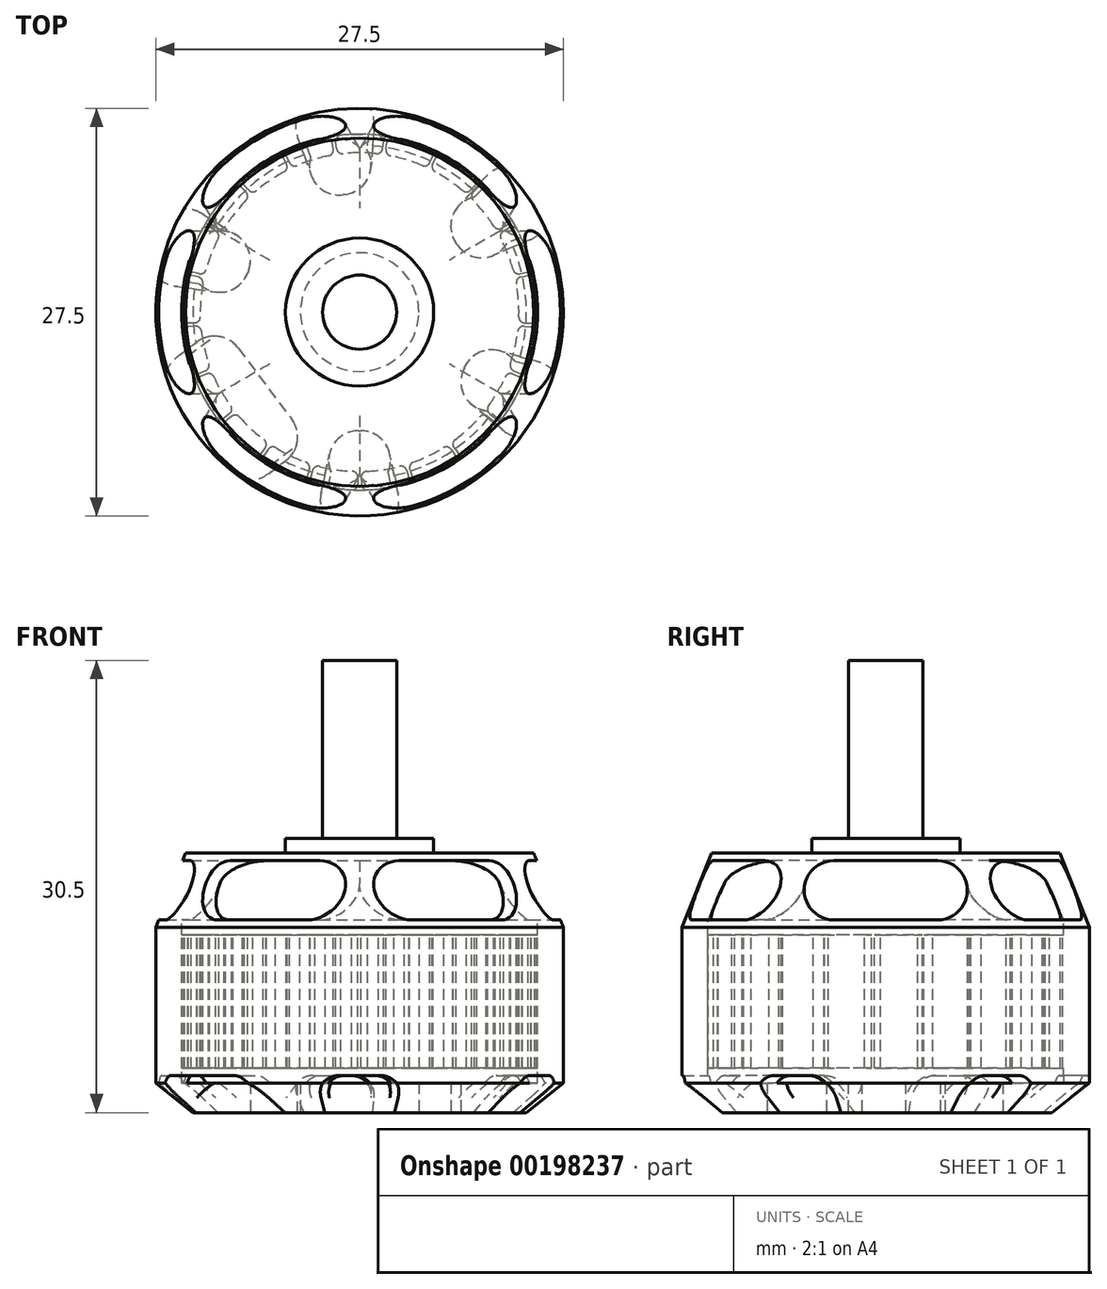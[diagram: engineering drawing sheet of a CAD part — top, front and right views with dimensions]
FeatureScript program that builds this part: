
annotation { "Feature Type Name" : "Feature", "Feature Type Description" : "" }
export const myFeature = defineFeature(function(context is Context, id is Id, definition is map)
    precondition{}
    {
        {
            var Q0;
            Q0=qCreatedBy(makeId("Top.planeOp"),FACE);
            var sketch = newSketch(context, id + "F0", { "sketchPlane" : qUnion([Q0])});
            skCircle(sketch, "E0", {"center": v(0, 0) * mm, "radius": 13.75 * mm});
            skSolve(sketch);
        }
        {
            var Q0;
            Q0=makeQuery(id+"F0.imprint","IMPRINT",FACE,{"disambiguationData":[TD([[makeQuery(id+"F0.imprint","IMPRINT",EDGE,{"derivedFrom":sQuery(id+"F0.wireOp",EDGE,"E0")}),1.0]])]});
            extrude(context, id + "F1", {"entities" : qUnion([Q0]), "depth" : 17.5 * mm});
        }
        {
            var Q0;
            Q0=makeQuery(id+"F1.opExtrude","CAP_FACE",FACE,{"disambiguationData":[OSD([sQuery(id+"F0.wireOp",EDGE,"E0")])],"isStart":false});
            var sketch = newSketch(context, id + "F2", { "sketchPlane" : qUnion([Q0])});
            skCircle(sketch, "E1", {"center": v(0, 0) * mm, "radius": 5 * mm});
            skSolve(sketch);
        }
        {
            var Q0;
            Q0=makeQuery(id+"F2.imprint","IMPRINT",FACE,{"disambiguationData":[TD([[makeQuery(id+"F2.imprint","IMPRINT",EDGE,{"derivedFrom":sQuery(id+"F2.wireOp",EDGE,"E1")}),1.0]])]});
            extrude(context, id + "F3", {"entities" : qUnion([Q0]), "operationType" : NewBodyOperationType.ADD, "depth" : 1 * mm});
        }
        {
            var Q0;
            Q0=makeQuery(id+"F3.opExtrude","CAP_FACE",FACE,{"disambiguationData":[OSD([sQuery(id+"F2.wireOp",EDGE,"E1")])],"isStart":false});
            var sketch = newSketch(context, id + "F4", { "sketchPlane" : qUnion([Q0])});
            skCircle(sketch, "E2", {"center": v(0, 0) * mm, "radius": 2.5 * mm});
            skSolve(sketch);
        }
        {
            var Q0;
            Q0=makeQuery(id+"F4.imprint","IMPRINT",FACE,{"disambiguationData":[TD([[makeQuery(id+"F4.imprint","IMPRINT",EDGE,{"derivedFrom":sQuery(id+"F4.wireOp",EDGE,"E2")}),1.0]])]});
            extrude(context, id + "F5", {"entities" : qUnion([Q0]), "operationType" : NewBodyOperationType.ADD, "depth" : 12 * mm});
        }
        {
            var Q0;
            Q0=makeQuery(id+"F1.opExtrude","CAP_EDGE",EDGE,{"disambiguationData":[OSD([sQuery(id+"F0.wireOp",EDGE,"E0")])],"isStart":false});
            chamfer(context, id + "F6", {"entities" : qUnion([Q0]), "chamferType" : ChamferType.TWO_OFFSETS, "width1" : 2 * mm, "oppositeDirection" : false, "width2" : 5 * mm, "tangentPropagation" : true});
        }
        {
            var Q0;
            Q0=makeQuery(id+"F1.opExtrude","CAP_EDGE",EDGE,{"disambiguationData":[OSD([sQuery(id+"F0.wireOp",EDGE,"E0")])],"isStart":true});
            chamfer(context, id + "F7", {"entities" : qUnion([Q0]), "chamferType" : ChamferType.TWO_OFFSETS, "width1" : 2 * mm, "oppositeDirection" : false, "width2" : 2.5 * mm, "tangentPropagation" : true});
        }
        {
            var Q0;
            Q0=qCreatedBy(makeId("Right.planeOp"),FACE);
            var sketch = newSketch(context, id + "F8", { "sketchPlane" : qUnion([Q0])});
            skLineSegment(sketch, "E3.bottom", {"start": v(-3.5, 17) * mm, "end": v(3.5, 17) * mm});
            skLineSegment(sketch, "E3.top", {"start": v(-3.5, 13) * mm, "end": v(3.5, 13) * mm});
            skLineSegment(sketch, "E3.left", {"start": v(-3.5, 17) * mm, "end": v(-3.5, 13) * mm, "construction": true});
            skLineSegment(sketch, "E3.right", {"start": v(3.5, 17) * mm, "end": v(3.5, 13) * mm, "construction": true});
            skArc(sketch, "E4", {"start": v(-3.5, 17) * mm, "mid": v(-5.5, 15) * mm, "end": v(-3.5, 13) * mm});
            skArc(sketch, "E5", {"start": v(3.5, 13) * mm, "mid": v(5.5, 15) * mm, "end": v(3.5, 17) * mm});
            skSolve(sketch);
        }
        {
            var Q0;
            Q0 = qSketchRegion(id + "F8", true);
            extrude(context, id + "F9", {"entities" : qUnion([Q0]), "endBound" : BoundingType.SYMMETRIC, "oppositeDirection" : true, "depth" : 30 * mm});
        }
        {
            var Q0;
            Q0=makeQuery(id+"F9.opExtrude","SWEPT_BODY",BODY,{"disambiguationData":[OSD([sQuery(id+"F8.wireOp",EDGE,"E3.bottom"),sQuery(id+"F8.wireOp",EDGE,"E3.top"),sQuery(id+"F8.wireOp",EDGE,"E4"),sQuery(id+"F8.wireOp",EDGE,"E5")])]});
            var Q1;
            Q1=makeQuery(id+"F5.opExtrude","SWEPT_FACE",FACE,{"disambiguationData":[OSD([sQuery(id+"F4.wireOp",EDGE,"E2")])]});
            circularPattern(context, id + "F10", {"entities" : qUnion([Q0]), "axis" : qUnion([Q1]), "angle" : 180 * degree, "instanceCount" : 4, "equalSpace" : true});
        }
        {
            var Q0;
            Q0=makeQuery(id+"F10.opPattern","COPY",BODY,{"derivedFrom":makeQuery(id+"F9.opExtrude","SWEPT_BODY",BODY,{"disambiguationData":[OSD([sQuery(id+"F8.wireOp",EDGE,"E3.bottom"),sQuery(id+"F8.wireOp",EDGE,"E3.top"),sQuery(id+"F8.wireOp",EDGE,"E4"),sQuery(id+"F8.wireOp",EDGE,"E5")])]}),"instanceName":"1"});
            var Q1;
            Q1=makeQuery(id+"F10.opPattern","COPY",BODY,{"derivedFrom":makeQuery(id+"F9.opExtrude","SWEPT_BODY",BODY,{"disambiguationData":[OSD([sQuery(id+"F8.wireOp",EDGE,"E3.bottom"),sQuery(id+"F8.wireOp",EDGE,"E3.top"),sQuery(id+"F8.wireOp",EDGE,"E4"),sQuery(id+"F8.wireOp",EDGE,"E5")])]}),"instanceName":"2"});
            var Q2;
            Q2=makeQuery(id+"F9.opExtrude","SWEPT_BODY",BODY,{"disambiguationData":[OSD([sQuery(id+"F8.wireOp",EDGE,"E3.bottom"),sQuery(id+"F8.wireOp",EDGE,"E3.top"),sQuery(id+"F8.wireOp",EDGE,"E4"),sQuery(id+"F8.wireOp",EDGE,"E5")])]});
            var Q3;
            Q3=makeQuery(id+"F10.opPattern","COPY",BODY,{"derivedFrom":makeQuery(id+"F9.opExtrude","SWEPT_BODY",BODY,{"disambiguationData":[OSD([sQuery(id+"F8.wireOp",EDGE,"E3.bottom"),sQuery(id+"F8.wireOp",EDGE,"E3.top"),sQuery(id+"F8.wireOp",EDGE,"E4"),sQuery(id+"F8.wireOp",EDGE,"E5")])]}),"instanceName":"3"});
            booleanBodies(context, id + "F11", {"operationType" : BooleanOperationType.UNION, "tools" : qUnion([Q0, Q1, Q2, Q3])});
        }
        {
            var Q0;
            Q0=makeQuery(id+"F9.opExtrude","SWEPT_BODY",BODY,{"disambiguationData":[OSD([sQuery(id+"F8.wireOp",EDGE,"E3.bottom"),sQuery(id+"F8.wireOp",EDGE,"E3.top"),sQuery(id+"F8.wireOp",EDGE,"E4"),sQuery(id+"F8.wireOp",EDGE,"E5")])]});
            var Q1;
            Q1=makeQuery(id+"F10.opPattern","COPY",BODY,{"derivedFrom":makeQuery(id+"F9.opExtrude","SWEPT_BODY",BODY,{"disambiguationData":[OSD([sQuery(id+"F8.wireOp",EDGE,"E3.bottom"),sQuery(id+"F8.wireOp",EDGE,"E3.top"),sQuery(id+"F8.wireOp",EDGE,"E4"),sQuery(id+"F8.wireOp",EDGE,"E5")])]}),"instanceName":"1"});
            var Q2;
            Q2=makeQuery(id+"F10.opPattern","COPY",BODY,{"derivedFrom":makeQuery(id+"F9.opExtrude","SWEPT_BODY",BODY,{"disambiguationData":[OSD([sQuery(id+"F8.wireOp",EDGE,"E3.bottom"),sQuery(id+"F8.wireOp",EDGE,"E3.top"),sQuery(id+"F8.wireOp",EDGE,"E4"),sQuery(id+"F8.wireOp",EDGE,"E5")])]}),"instanceName":"2"});
            var Q3;
            Q3=makeQuery(id+"F1.opExtrude","SWEPT_BODY",BODY,{"disambiguationData":[OSD([sQuery(id+"F0.wireOp",EDGE,"E0")])]});
            booleanBodies(context, id + "F12", {"operationType" : BooleanOperationType.SUBTRACTION, "tools" : qUnion([Q0, Q1, Q2]), "targets" : qUnion([Q3])});
        }
        {
            var Q0;
            Q0=qCreatedBy(makeId("Right.planeOp"),FACE);
            var sketch = newSketch(context, id + "F13", { "sketchPlane" : qUnion([Q0])});
            skLineSegment(sketch, "E6", {"start": v(10.9, 15.44) * mm, "end": v(12, 13) * mm});
            skLineSegment(sketch, "E7", {"start": v(12, 13) * mm, "end": v(12, 2) * mm});
            skLineSegment(sketch, "E8", {"start": v(12, 2) * mm, "end": v(0, 2) * mm});
            skLineSegment(sketch, "E9", {"start": v(0, 2) * mm, "end": v(0, 15.44) * mm});
            skLineSegment(sketch, "E10", {"start": v(0, 15.44) * mm, "end": v(10.9, 15.44) * mm});
            skSolve(sketch);
        }
        {
            var Q0;
            Q0 = qSketchRegion(id + "F13", true);
            var Q1;
            Q1=sQuery(id+"F13.wireOp",EDGE,"E9");
            revolve(context, id + "F14", {"operationType" : NewBodyOperationType.REMOVE, "entities" : qUnion([Q0]), "axis" : qUnion([Q1]), "revolveType" : RevolveType.FULL, "oppositeDirection" : true});
        }
        {
            var Q0;
            Q0=qCreatedBy(makeId("Top.planeOp"),FACE);
            cPlane(context, id + "F15", {"entities" : qUnion([Q0]), "cplaneType" : CPlaneType.OFFSET, "offset" : 12 * mm, "width" : 150 * mm, "height" : 150 * mm});
        }
        {
            var Q0;
            Q0=qCreatedBy(id+"F15.planeOp",FACE);
            var sketch = newSketch(context, id + "F16", { "sketchPlane" : qUnion([Q0])});
            skArc(sketch, "E11", {"start": v(1.26, 11.93) * mm, "mid": v(0, 12) * mm, "end": v(-1.26, 11.93) * mm});
            skArc(sketch, "E12", {"start": v(1.11, 10.7) * mm, "mid": v(0, 10.75) * mm, "end": v(-1.11, 10.7) * mm});
            skLineSegment(sketch, "E13", {"start": v(1.55, 11.03) * mm, "end": v(1.61, 11.48) * mm});
            skLineSegment(sketch, "E14", {"start": v(-1.55, 11.03) * mm, "end": v(-1.61, 11.48) * mm});
            skPoint(sketch, "E15.visualSharp", {"position": v(-1.5, 10.65) * mm});
            skArc(sketch, "E15.filletArc", {"start": v(-1.55, 11.03) * mm, "mid": v(-1.4, 10.77) * mm, "end": v(-1.11, 10.7) * mm});
            skPoint(sketch, "E16.visualSharp", {"position": v(1.5, 10.65) * mm});
            skArc(sketch, "E16.filletArc", {"start": v(1.11, 10.7) * mm, "mid": v(1.4, 10.77) * mm, "end": v(1.55, 11.03) * mm});
            skPoint(sketch, "E17.visualSharp", {"position": v(-1.67, 11.88) * mm});
            skArc(sketch, "E17.filletArc", {"start": v(-1.26, 11.93) * mm, "mid": v(-1.53, 11.78) * mm, "end": v(-1.61, 11.48) * mm});
            skPoint(sketch, "E18.visualSharp", {"position": v(1.67, 11.88) * mm});
            skArc(sketch, "E18.filletArc", {"start": v(1.61, 11.48) * mm, "mid": v(1.53, 11.78) * mm, "end": v(1.26, 11.93) * mm});
            skPoint(sketch, "E19.1.0", {"position": v(-1.7, 10.61) * mm});
            skPoint(sketch, "E19.1.1", {"position": v(-4.57, 9.73) * mm});
            skPoint(sketch, "E19.1.2", {"position": v(-1.9, 11.85) * mm});
            skPoint(sketch, "E19.1.3", {"position": v(-5.1, 10.86) * mm});
            skArc(sketch, "E19.1.4", {"start": v(-2.31, 11.77) * mm, "mid": v(-3.54, 11.47) * mm, "end": v(-4.72, 11.03) * mm});
            skArc(sketch, "E19.1.5", {"start": v(-2.09, 10.55) * mm, "mid": v(-3.17, 10.27) * mm, "end": v(-4.22, 9.89) * mm});
            skLineSegment(sketch, "E19.1.6", {"start": v(-1.77, 11) * mm, "end": v(-1.84, 11.45) * mm});
            skArc(sketch, "E19.1.7", {"start": v(-4.72, 11.03) * mm, "mid": v(-4.94, 10.8) * mm, "end": v(-4.93, 10.5) * mm});
            skArc(sketch, "E19.1.8", {"start": v(-4.73, 10.09) * mm, "mid": v(-4.51, 9.88) * mm, "end": v(-4.22, 9.89) * mm});
            skArc(sketch, "E19.1.9", {"start": v(-1.84, 11.45) * mm, "mid": v(-2, 11.71) * mm, "end": v(-2.31, 11.77) * mm});
            skLineSegment(sketch, "E19.1.10", {"start": v(-4.73, 10.09) * mm, "end": v(-4.93, 10.5) * mm});
            skArc(sketch, "E19.1.11", {"start": v(-2.09, 10.55) * mm, "mid": v(-1.84, 10.7) * mm, "end": v(-1.77, 11) * mm});
            skPoint(sketch, "E19.2.0", {"position": v(-4.76, 9.64) * mm});
            skPoint(sketch, "E19.2.1", {"position": v(-7.23, 7.95) * mm});
            skPoint(sketch, "E19.2.2", {"position": v(-5.31, 10.76) * mm});
            skPoint(sketch, "E19.2.3", {"position": v(-8.07, 8.88) * mm});
            skArc(sketch, "E19.2.4", {"start": v(-5.68, 10.57) * mm, "mid": v(-6.76, 9.91) * mm, "end": v(-7.76, 9.15) * mm});
            skArc(sketch, "E19.2.5", {"start": v(-5.1, 9.46) * mm, "mid": v(-6.06, 8.88) * mm, "end": v(-6.94, 8.2) * mm});
            skLineSegment(sketch, "E19.2.6", {"start": v(-4.93, 10) * mm, "end": v(-5.13, 10.4) * mm});
            skArc(sketch, "E19.2.7", {"start": v(-7.76, 9.15) * mm, "mid": v(-7.9, 8.87) * mm, "end": v(-7.8, 8.58) * mm});
            skArc(sketch, "E19.2.8", {"start": v(-7.5, 8.24) * mm, "mid": v(-7.23, 8.11) * mm, "end": v(-6.94, 8.2) * mm});
            skArc(sketch, "E19.2.9", {"start": v(-5.13, 10.4) * mm, "mid": v(-5.37, 10.6) * mm, "end": v(-5.68, 10.57) * mm});
            skLineSegment(sketch, "E19.2.10", {"start": v(-7.5, 8.24) * mm, "end": v(-7.8, 8.58) * mm});
            skArc(sketch, "E19.2.11", {"start": v(-5.1, 9.46) * mm, "mid": v(-4.91, 9.7) * mm, "end": v(-4.93, 10) * mm});
            skPoint(sketch, "E19.3.0", {"position": v(-7.4, 7.8) * mm});
            skPoint(sketch, "E19.3.1", {"position": v(-9.26, 5.47) * mm});
            skPoint(sketch, "E19.3.2", {"position": v(-8.25, 8.71) * mm});
            skPoint(sketch, "E19.3.3", {"position": v(-10.33, 6.1) * mm});
            skArc(sketch, "E19.3.4", {"start": v(-8.55, 8.43) * mm, "mid": v(-9.38, 7.48) * mm, "end": v(-10.12, 6.46) * mm});
            skArc(sketch, "E19.3.5", {"start": v(-7.67, 7.54) * mm, "mid": v(-8.4, 6.7) * mm, "end": v(-9.05, 5.8) * mm});
            skLineSegment(sketch, "E19.3.6", {"start": v(-7.66, 8.1) * mm, "end": v(-7.97, 8.42) * mm});
            skArc(sketch, "E19.3.7", {"start": v(-10.12, 6.46) * mm, "mid": v(-10.17, 6.15) * mm, "end": v(-9.98, 5.9) * mm});
            skArc(sketch, "E19.3.8", {"start": v(-9.6, 5.67) * mm, "mid": v(-9.3, 5.62) * mm, "end": v(-9.05, 5.8) * mm});
            skArc(sketch, "E19.3.9", {"start": v(-7.97, 8.42) * mm, "mid": v(-8.26, 8.54) * mm, "end": v(-8.55, 8.43) * mm});
            skLineSegment(sketch, "E19.3.10", {"start": v(-9.6, 5.67) * mm, "end": v(-9.98, 5.9) * mm});
            skArc(sketch, "E19.3.11", {"start": v(-7.67, 7.54) * mm, "mid": v(-7.55, 7.81) * mm, "end": v(-7.66, 8.1) * mm});
            skPoint(sketch, "E19.4.0", {"position": v(-9.36, 5.28) * mm});
            skPoint(sketch, "E19.4.1", {"position": v(-10.46, 2.5) * mm});
            skPoint(sketch, "E19.4.2", {"position": v(-10.45, 5.9) * mm});
            skPoint(sketch, "E19.4.3", {"position": v(-11.67, 2.79) * mm});
            skArc(sketch, "E19.4.4", {"start": v(-10.65, 5.53) * mm, "mid": v(-11.17, 4.38) * mm, "end": v(-11.57, 3.19) * mm});
            skArc(sketch, "E19.4.5", {"start": v(-9.55, 4.94) * mm, "mid": v(-10, 3.93) * mm, "end": v(-10.36, 2.87) * mm});
            skLineSegment(sketch, "E19.4.6", {"start": v(-9.7, 5.47) * mm, "end": v(-10.1, 5.7) * mm});
            skArc(sketch, "E19.4.7", {"start": v(-11.57, 3.19) * mm, "mid": v(-11.53, 2.88) * mm, "end": v(-11.28, 2.7) * mm});
            skArc(sketch, "E19.4.8", {"start": v(-10.84, 2.59) * mm, "mid": v(-10.54, 2.63) * mm, "end": v(-10.36, 2.87) * mm});
            skArc(sketch, "E19.4.9", {"start": v(-10.1, 5.7) * mm, "mid": v(-10.4, 5.73) * mm, "end": v(-10.65, 5.53) * mm});
            skLineSegment(sketch, "E19.4.10", {"start": v(-10.84, 2.59) * mm, "end": v(-11.28, 2.7) * mm});
            skArc(sketch, "E19.4.11", {"start": v(-9.55, 4.94) * mm, "mid": v(-9.52, 5.24) * mm, "end": v(-9.7, 5.47) * mm});
            skPoint(sketch, "E19.5.0", {"position": v(-10.5, 2.29) * mm});
            skPoint(sketch, "E19.5.1", {"position": v(-10.73, -0.7) * mm});
            skPoint(sketch, "E19.5.2", {"position": v(-11.73, 2.55) * mm});
            skPoint(sketch, "E19.5.3", {"position": v(-11.97, -0.78) * mm});
            skArc(sketch, "E19.5.4", {"start": v(-11.8, 2.15) * mm, "mid": v(-11.97, 0.9) * mm, "end": v(-12, -0.36) * mm});
            skArc(sketch, "E19.5.5", {"start": v(-10.58, 1.9) * mm, "mid": v(-10.72, 0.8) * mm, "end": v(-10.75, -0.31) * mm});
            skLineSegment(sketch, "E19.5.6", {"start": v(-10.89, 2.37) * mm, "end": v(-11.33, 2.47) * mm});
            skArc(sketch, "E19.5.7", {"start": v(-12, -0.36) * mm, "mid": v(-11.86, -0.65) * mm, "end": v(-11.57, -0.75) * mm});
            skArc(sketch, "E19.5.8", {"start": v(-11.12, -0.72) * mm, "mid": v(-10.85, -0.6) * mm, "end": v(-10.75, -0.31) * mm});
            skArc(sketch, "E19.5.9", {"start": v(-11.33, 2.47) * mm, "mid": v(-11.63, 2.4) * mm, "end": v(-11.8, 2.15) * mm});
            skLineSegment(sketch, "E19.5.10", {"start": v(-11.12, -0.72) * mm, "end": v(-11.57, -0.75) * mm});
            skArc(sketch, "E19.5.11", {"start": v(-10.58, 1.9) * mm, "mid": v(-10.64, 2.2) * mm, "end": v(-10.89, 2.37) * mm});
            skPoint(sketch, "E19.6.0", {"position": v(-10.71, -0.91) * mm});
            skPoint(sketch, "E19.6.1", {"position": v(-10.05, -3.83) * mm});
            skPoint(sketch, "E19.6.2", {"position": v(-11.96, -1.02) * mm});
            skPoint(sketch, "E19.6.3", {"position": v(-11.21, -4.27) * mm});
            skArc(sketch, "E19.6.4", {"start": v(-11.91, -1.43) * mm, "mid": v(-11.7, -2.67) * mm, "end": v(-11.35, -3.88) * mm});
            skArc(sketch, "E19.6.5", {"start": v(-10.67, -1.3) * mm, "mid": v(-10.48, -2.4) * mm, "end": v(-10.18, -3.46) * mm});
            skLineSegment(sketch, "E19.6.6", {"start": v(-11.1, -0.94) * mm, "end": v(-11.55, -0.98) * mm});
            skArc(sketch, "E19.6.7", {"start": v(-11.35, -3.88) * mm, "mid": v(-11.15, -4.12) * mm, "end": v(-10.83, -4.13) * mm});
            skArc(sketch, "E19.6.8", {"start": v(-10.41, -3.97) * mm, "mid": v(-10.2, -3.76) * mm, "end": v(-10.18, -3.46) * mm});
            skArc(sketch, "E19.6.9", {"start": v(-11.55, -0.98) * mm, "mid": v(-11.83, -1.13) * mm, "end": v(-11.91, -1.43) * mm});
            skLineSegment(sketch, "E19.6.10", {"start": v(-10.41, -3.97) * mm, "end": v(-10.83, -4.13) * mm});
            skArc(sketch, "E19.6.11", {"start": v(-10.67, -1.3) * mm, "mid": v(-10.82, -1.03) * mm, "end": v(-11.1, -0.94) * mm});
            skPoint(sketch, "E19.7.0", {"position": v(-9.97, -4.03) * mm});
            skPoint(sketch, "E19.7.1", {"position": v(-8.47, -6.62) * mm});
            skPoint(sketch, "E19.7.2", {"position": v(-11.13, -4.5) * mm});
            skPoint(sketch, "E19.7.3", {"position": v(-9.46, -7.39) * mm});
            skArc(sketch, "E19.7.4", {"start": v(-10.96, -4.88) * mm, "mid": v(-10.4, -6) * mm, "end": v(-9.7, -7.06) * mm});
            skArc(sketch, "E19.7.5", {"start": v(-9.82, -4.38) * mm, "mid": v(-9.3, -5.38) * mm, "end": v(-8.7, -6.31) * mm});
            skLineSegment(sketch, "E19.7.6", {"start": v(-10.33, -4.17) * mm, "end": v(-10.75, -4.34) * mm});
            skArc(sketch, "E19.7.7", {"start": v(-9.7, -7.06) * mm, "mid": v(-9.44, -7.22) * mm, "end": v(-9.14, -7.14) * mm});
            skArc(sketch, "E19.7.8", {"start": v(-8.78, -6.86) * mm, "mid": v(-8.63, -6.6) * mm, "end": v(-8.7, -6.31) * mm});
            skArc(sketch, "E19.7.9", {"start": v(-10.75, -4.34) * mm, "mid": v(-10.97, -4.56) * mm, "end": v(-10.96, -4.88) * mm});
            skLineSegment(sketch, "E19.7.10", {"start": v(-8.78, -6.86) * mm, "end": v(-9.14, -7.14) * mm});
            skArc(sketch, "E19.7.11", {"start": v(-9.82, -4.38) * mm, "mid": v(-10.03, -4.17) * mm, "end": v(-10.33, -4.17) * mm});
            skPoint(sketch, "E19.8.0", {"position": v(-8.34, -6.79) * mm});
            skPoint(sketch, "E19.8.1", {"position": v(-6.14, -8.82) * mm});
            skPoint(sketch, "E19.8.2", {"position": v(-9.3, -7.58) * mm});
            skPoint(sketch, "E19.8.3", {"position": v(-6.86, -9.85) * mm});
            skArc(sketch, "E19.8.4", {"start": v(-9.04, -7.9) * mm, "mid": v(-8.16, -8.8) * mm, "end": v(-7.2, -9.6) * mm});
            skArc(sketch, "E19.8.5", {"start": v(-8.09, -7.08) * mm, "mid": v(-7.31, -7.88) * mm, "end": v(-6.46, -8.6) * mm});
            skLineSegment(sketch, "E19.8.6", {"start": v(-8.64, -7.03) * mm, "end": v(-9, -7.32) * mm});
            skArc(sketch, "E19.8.7", {"start": v(-7.2, -9.6) * mm, "mid": v(-6.9, -9.68) * mm, "end": v(-6.63, -9.51) * mm});
            skArc(sketch, "E19.8.8", {"start": v(-6.37, -9.14) * mm, "mid": v(-6.3, -8.85) * mm, "end": v(-6.46, -8.6) * mm});
            skArc(sketch, "E19.8.9", {"start": v(-9, -7.32) * mm, "mid": v(-9.14, -7.6) * mm, "end": v(-9.04, -7.9) * mm});
            skLineSegment(sketch, "E19.8.10", {"start": v(-6.37, -9.14) * mm, "end": v(-6.63, -9.51) * mm});
            skArc(sketch, "E19.8.11", {"start": v(-8.09, -7.08) * mm, "mid": v(-8.36, -6.95) * mm, "end": v(-8.64, -7.03) * mm});
            skPoint(sketch, "E19.9.0", {"position": v(-5.97, -8.94) * mm});
            skPoint(sketch, "E19.9.1", {"position": v(-3.27, -10.24) * mm});
            skPoint(sketch, "E19.9.2", {"position": v(-6.66, -9.98) * mm});
            skPoint(sketch, "E19.9.3", {"position": v(-3.65, -11.43) * mm});
            skArc(sketch, "E19.9.4", {"start": v(-6.31, -10.2) * mm, "mid": v(-5.2, -10.81) * mm, "end": v(-4.04, -11.3) * mm});
            skArc(sketch, "E19.9.5", {"start": v(-5.64, -9.15) * mm, "mid": v(-4.66, -9.69) * mm, "end": v(-3.64, -10.12) * mm});
            skLineSegment(sketch, "E19.9.6", {"start": v(-6.18, -9.27) * mm, "end": v(-6.43, -9.64) * mm});
            skArc(sketch, "E19.9.7", {"start": v(-4.04, -11.3) * mm, "mid": v(-3.73, -11.28) * mm, "end": v(-3.53, -11.04) * mm});
            skArc(sketch, "E19.9.8", {"start": v(-3.4, -10.61) * mm, "mid": v(-3.41, -10.32) * mm, "end": v(-3.64, -10.12) * mm});
            skArc(sketch, "E19.9.9", {"start": v(-6.43, -9.64) * mm, "mid": v(-6.5, -9.95) * mm, "end": v(-6.31, -10.2) * mm});
            skLineSegment(sketch, "E19.9.10", {"start": v(-3.4, -10.61) * mm, "end": v(-3.53, -11.04) * mm});
            skArc(sketch, "E19.9.11", {"start": v(-5.64, -9.15) * mm, "mid": v(-5.94, -9.1) * mm, "end": v(-6.18, -9.27) * mm});
            skPoint(sketch, "E19.10.0", {"position": v(-3.07, -10.3) * mm});
            skPoint(sketch, "E19.10.1", {"position": v(-0.1, -10.75) * mm});
            skPoint(sketch, "E19.10.2", {"position": v(-3.42, -11.5) * mm});
            skPoint(sketch, "E19.10.3", {"position": v(-0.12, -12) * mm});
            skArc(sketch, "E19.10.4", {"start": v(-3.02, -11.61) * mm, "mid": v(-1.79, -11.87) * mm, "end": v(-0.53, -11.99) * mm});
            skArc(sketch, "E19.10.5", {"start": v(-2.7, -10.4) * mm, "mid": v(-1.6, -10.63) * mm, "end": v(-0.5, -10.74) * mm});
            skLineSegment(sketch, "E19.10.6", {"start": v(-3.18, -10.68) * mm, "end": v(-3.3, -11.11) * mm});
            skArc(sketch, "E19.10.7", {"start": v(-0.53, -11.99) * mm, "mid": v(-0.24, -11.88) * mm, "end": v(-0.12, -11.6) * mm});
            skArc(sketch, "E19.10.8", {"start": v(-0.11, -11.14) * mm, "mid": v(-0.22, -10.86) * mm, "end": v(-0.5, -10.74) * mm});
            skArc(sketch, "E19.10.9", {"start": v(-3.3, -11.11) * mm, "mid": v(-3.27, -11.42) * mm, "end": v(-3.02, -11.61) * mm});
            skLineSegment(sketch, "E19.10.10", {"start": v(-0.11, -11.14) * mm, "end": v(-0.12, -11.6) * mm});
            skArc(sketch, "E19.10.11", {"start": v(-2.7, -10.4) * mm, "mid": v(-3, -10.45) * mm, "end": v(-3.18, -10.68) * mm});
            skPoint(sketch, "E19.11.0", {"position": v(0.1, -10.75) * mm});
            skPoint(sketch, "E19.11.1", {"position": v(3.07, -10.3) * mm});
            skPoint(sketch, "E19.11.2", {"position": v(0.12, -12) * mm});
            skPoint(sketch, "E19.11.3", {"position": v(3.42, -11.5) * mm});
            skArc(sketch, "E19.11.4", {"start": v(0.53, -11.99) * mm, "mid": v(1.79, -11.87) * mm, "end": v(3.02, -11.61) * mm});
            skArc(sketch, "E19.11.5", {"start": v(0.5, -10.74) * mm, "mid": v(1.6, -10.63) * mm, "end": v(2.7, -10.4) * mm});
            skLineSegment(sketch, "E19.11.6", {"start": v(0.11, -11.14) * mm, "end": v(0.12, -11.6) * mm});
            skArc(sketch, "E19.11.7", {"start": v(3.02, -11.61) * mm, "mid": v(3.27, -11.42) * mm, "end": v(3.3, -11.11) * mm});
            skArc(sketch, "E19.11.8", {"start": v(3.18, -10.68) * mm, "mid": v(3, -10.45) * mm, "end": v(2.7, -10.4) * mm});
            skArc(sketch, "E19.11.9", {"start": v(0.12, -11.6) * mm, "mid": v(0.24, -11.88) * mm, "end": v(0.53, -11.99) * mm});
            skLineSegment(sketch, "E19.11.10", {"start": v(3.18, -10.68) * mm, "end": v(3.3, -11.11) * mm});
            skArc(sketch, "E19.11.11", {"start": v(0.5, -10.74) * mm, "mid": v(0.22, -10.86) * mm, "end": v(0.11, -11.14) * mm});
            skPoint(sketch, "E19.12.0", {"position": v(3.27, -10.24) * mm});
            skPoint(sketch, "E19.12.1", {"position": v(5.97, -8.94) * mm});
            skPoint(sketch, "E19.12.2", {"position": v(3.65, -11.43) * mm});
            skPoint(sketch, "E19.12.3", {"position": v(6.66, -9.98) * mm});
            skArc(sketch, "E19.12.4", {"start": v(4.04, -11.3) * mm, "mid": v(5.2, -10.81) * mm, "end": v(6.31, -10.2) * mm});
            skArc(sketch, "E19.12.5", {"start": v(3.64, -10.12) * mm, "mid": v(4.66, -9.69) * mm, "end": v(5.64, -9.15) * mm});
            skLineSegment(sketch, "E19.12.6", {"start": v(3.4, -10.61) * mm, "end": v(3.53, -11.04) * mm});
            skArc(sketch, "E19.12.7", {"start": v(6.31, -10.2) * mm, "mid": v(6.5, -9.95) * mm, "end": v(6.43, -9.64) * mm});
            skArc(sketch, "E19.12.8", {"start": v(6.18, -9.27) * mm, "mid": v(5.94, -9.1) * mm, "end": v(5.64, -9.15) * mm});
            skArc(sketch, "E19.12.9", {"start": v(3.53, -11.04) * mm, "mid": v(3.73, -11.28) * mm, "end": v(4.04, -11.3) * mm});
            skLineSegment(sketch, "E19.12.10", {"start": v(6.18, -9.27) * mm, "end": v(6.43, -9.64) * mm});
            skArc(sketch, "E19.12.11", {"start": v(3.64, -10.12) * mm, "mid": v(3.41, -10.32) * mm, "end": v(3.4, -10.61) * mm});
            skPoint(sketch, "E19.13.0", {"position": v(6.14, -8.82) * mm});
            skPoint(sketch, "E19.13.1", {"position": v(8.34, -6.79) * mm});
            skPoint(sketch, "E19.13.2", {"position": v(6.86, -9.85) * mm});
            skPoint(sketch, "E19.13.3", {"position": v(9.3, -7.58) * mm});
            skArc(sketch, "E19.13.4", {"start": v(7.2, -9.6) * mm, "mid": v(8.16, -8.8) * mm, "end": v(9.04, -7.9) * mm});
            skArc(sketch, "E19.13.5", {"start": v(6.46, -8.6) * mm, "mid": v(7.31, -7.88) * mm, "end": v(8.09, -7.08) * mm});
            skLineSegment(sketch, "E19.13.6", {"start": v(6.37, -9.14) * mm, "end": v(6.63, -9.51) * mm});
            skArc(sketch, "E19.13.7", {"start": v(9.04, -7.9) * mm, "mid": v(9.14, -7.6) * mm, "end": v(9, -7.32) * mm});
            skArc(sketch, "E19.13.8", {"start": v(8.64, -7.03) * mm, "mid": v(8.36, -6.95) * mm, "end": v(8.09, -7.08) * mm});
            skArc(sketch, "E19.13.9", {"start": v(6.63, -9.51) * mm, "mid": v(6.9, -9.68) * mm, "end": v(7.2, -9.6) * mm});
            skLineSegment(sketch, "E19.13.10", {"start": v(8.64, -7.03) * mm, "end": v(9, -7.32) * mm});
            skArc(sketch, "E19.13.11", {"start": v(6.46, -8.6) * mm, "mid": v(6.3, -8.85) * mm, "end": v(6.37, -9.14) * mm});
            skPoint(sketch, "E19.14.0", {"position": v(8.47, -6.62) * mm});
            skPoint(sketch, "E19.14.1", {"position": v(9.97, -4.03) * mm});
            skPoint(sketch, "E19.14.2", {"position": v(9.46, -7.39) * mm});
            skPoint(sketch, "E19.14.3", {"position": v(11.13, -4.5) * mm});
            skArc(sketch, "E19.14.4", {"start": v(9.7, -7.06) * mm, "mid": v(10.4, -6) * mm, "end": v(10.96, -4.88) * mm});
            skArc(sketch, "E19.14.5", {"start": v(8.7, -6.31) * mm, "mid": v(9.3, -5.38) * mm, "end": v(9.82, -4.38) * mm});
            skLineSegment(sketch, "E19.14.6", {"start": v(8.78, -6.86) * mm, "end": v(9.14, -7.14) * mm});
            skArc(sketch, "E19.14.7", {"start": v(10.96, -4.88) * mm, "mid": v(10.97, -4.56) * mm, "end": v(10.75, -4.34) * mm});
            skArc(sketch, "E19.14.8", {"start": v(10.33, -4.17) * mm, "mid": v(10.03, -4.17) * mm, "end": v(9.82, -4.38) * mm});
            skArc(sketch, "E19.14.9", {"start": v(9.14, -7.14) * mm, "mid": v(9.44, -7.22) * mm, "end": v(9.7, -7.06) * mm});
            skLineSegment(sketch, "E19.14.10", {"start": v(10.33, -4.17) * mm, "end": v(10.75, -4.34) * mm});
            skArc(sketch, "E19.14.11", {"start": v(8.7, -6.31) * mm, "mid": v(8.63, -6.6) * mm, "end": v(8.78, -6.86) * mm});
            skPoint(sketch, "E19.15.0", {"position": v(10.05, -3.83) * mm});
            skPoint(sketch, "E19.15.1", {"position": v(10.71, -0.91) * mm});
            skPoint(sketch, "E19.15.2", {"position": v(11.21, -4.27) * mm});
            skPoint(sketch, "E19.15.3", {"position": v(11.96, -1.02) * mm});
            skArc(sketch, "E19.15.4", {"start": v(11.35, -3.88) * mm, "mid": v(11.7, -2.67) * mm, "end": v(11.91, -1.43) * mm});
            skArc(sketch, "E19.15.5", {"start": v(10.18, -3.46) * mm, "mid": v(10.48, -2.4) * mm, "end": v(10.67, -1.3) * mm});
            skLineSegment(sketch, "E19.15.6", {"start": v(10.41, -3.97) * mm, "end": v(10.83, -4.13) * mm});
            skArc(sketch, "E19.15.7", {"start": v(11.91, -1.43) * mm, "mid": v(11.83, -1.13) * mm, "end": v(11.55, -0.98) * mm});
            skArc(sketch, "E19.15.8", {"start": v(11.1, -0.94) * mm, "mid": v(10.82, -1.03) * mm, "end": v(10.67, -1.3) * mm});
            skArc(sketch, "E19.15.9", {"start": v(10.83, -4.13) * mm, "mid": v(11.15, -4.12) * mm, "end": v(11.35, -3.88) * mm});
            skLineSegment(sketch, "E19.15.10", {"start": v(11.1, -0.94) * mm, "end": v(11.55, -0.98) * mm});
            skArc(sketch, "E19.15.11", {"start": v(10.18, -3.46) * mm, "mid": v(10.2, -3.76) * mm, "end": v(10.41, -3.97) * mm});
            skPoint(sketch, "E19.16.0", {"position": v(10.73, -0.7) * mm});
            skPoint(sketch, "E19.16.1", {"position": v(10.5, 2.29) * mm});
            skPoint(sketch, "E19.16.2", {"position": v(11.97, -0.78) * mm});
            skPoint(sketch, "E19.16.3", {"position": v(11.73, 2.55) * mm});
            skArc(sketch, "E19.16.4", {"start": v(12, -0.36) * mm, "mid": v(11.97, 0.9) * mm, "end": v(11.8, 2.15) * mm});
            skArc(sketch, "E19.16.5", {"start": v(10.75, -0.31) * mm, "mid": v(10.72, 0.8) * mm, "end": v(10.58, 1.9) * mm});
            skLineSegment(sketch, "E19.16.6", {"start": v(11.12, -0.72) * mm, "end": v(11.57, -0.75) * mm});
            skArc(sketch, "E19.16.7", {"start": v(11.8, 2.15) * mm, "mid": v(11.63, 2.4) * mm, "end": v(11.33, 2.47) * mm});
            skArc(sketch, "E19.16.8", {"start": v(10.89, 2.37) * mm, "mid": v(10.64, 2.2) * mm, "end": v(10.58, 1.9) * mm});
            skArc(sketch, "E19.16.9", {"start": v(11.57, -0.75) * mm, "mid": v(11.86, -0.65) * mm, "end": v(12, -0.36) * mm});
            skLineSegment(sketch, "E19.16.10", {"start": v(10.89, 2.37) * mm, "end": v(11.33, 2.47) * mm});
            skArc(sketch, "E19.16.11", {"start": v(10.75, -0.31) * mm, "mid": v(10.85, -0.6) * mm, "end": v(11.12, -0.72) * mm});
            skPoint(sketch, "E19.17.0", {"position": v(10.46, 2.5) * mm});
            skPoint(sketch, "E19.17.1", {"position": v(9.36, 5.28) * mm});
            skPoint(sketch, "E19.17.2", {"position": v(11.67, 2.79) * mm});
            skPoint(sketch, "E19.17.3", {"position": v(10.45, 5.9) * mm});
            skArc(sketch, "E19.17.4", {"start": v(11.57, 3.19) * mm, "mid": v(11.17, 4.38) * mm, "end": v(10.65, 5.53) * mm});
            skArc(sketch, "E19.17.5", {"start": v(10.36, 2.87) * mm, "mid": v(10, 3.93) * mm, "end": v(9.55, 4.94) * mm});
            skLineSegment(sketch, "E19.17.6", {"start": v(10.84, 2.59) * mm, "end": v(11.28, 2.7) * mm});
            skArc(sketch, "E19.17.7", {"start": v(10.65, 5.53) * mm, "mid": v(10.4, 5.73) * mm, "end": v(10.1, 5.7) * mm});
            skArc(sketch, "E19.17.8", {"start": v(9.7, 5.47) * mm, "mid": v(9.52, 5.24) * mm, "end": v(9.55, 4.94) * mm});
            skArc(sketch, "E19.17.9", {"start": v(11.28, 2.7) * mm, "mid": v(11.53, 2.88) * mm, "end": v(11.57, 3.19) * mm});
            skLineSegment(sketch, "E19.17.10", {"start": v(9.7, 5.47) * mm, "end": v(10.1, 5.7) * mm});
            skArc(sketch, "E19.17.11", {"start": v(10.36, 2.87) * mm, "mid": v(10.54, 2.63) * mm, "end": v(10.84, 2.59) * mm});
            skPoint(sketch, "E19.18.0", {"position": v(9.26, 5.47) * mm});
            skPoint(sketch, "E19.18.1", {"position": v(7.4, 7.8) * mm});
            skPoint(sketch, "E19.18.2", {"position": v(10.33, 6.1) * mm});
            skPoint(sketch, "E19.18.3", {"position": v(8.25, 8.71) * mm});
            skArc(sketch, "E19.18.4", {"start": v(10.12, 6.46) * mm, "mid": v(9.38, 7.48) * mm, "end": v(8.55, 8.43) * mm});
            skArc(sketch, "E19.18.5", {"start": v(9.05, 5.8) * mm, "mid": v(8.4, 6.7) * mm, "end": v(7.67, 7.54) * mm});
            skLineSegment(sketch, "E19.18.6", {"start": v(9.6, 5.67) * mm, "end": v(9.98, 5.9) * mm});
            skArc(sketch, "E19.18.7", {"start": v(8.55, 8.43) * mm, "mid": v(8.26, 8.54) * mm, "end": v(7.97, 8.42) * mm});
            skArc(sketch, "E19.18.8", {"start": v(7.66, 8.1) * mm, "mid": v(7.55, 7.81) * mm, "end": v(7.67, 7.54) * mm});
            skArc(sketch, "E19.18.9", {"start": v(9.98, 5.9) * mm, "mid": v(10.17, 6.15) * mm, "end": v(10.12, 6.46) * mm});
            skLineSegment(sketch, "E19.18.10", {"start": v(7.66, 8.1) * mm, "end": v(7.97, 8.42) * mm});
            skArc(sketch, "E19.18.11", {"start": v(9.05, 5.8) * mm, "mid": v(9.3, 5.62) * mm, "end": v(9.6, 5.67) * mm});
            skPoint(sketch, "E19.19.0", {"position": v(7.23, 7.95) * mm});
            skPoint(sketch, "E19.19.1", {"position": v(4.76, 9.64) * mm});
            skPoint(sketch, "E19.19.2", {"position": v(8.07, 8.88) * mm});
            skPoint(sketch, "E19.19.3", {"position": v(5.31, 10.76) * mm});
            skArc(sketch, "E19.19.4", {"start": v(7.76, 9.15) * mm, "mid": v(6.76, 9.91) * mm, "end": v(5.68, 10.57) * mm});
            skArc(sketch, "E19.19.5", {"start": v(6.94, 8.2) * mm, "mid": v(6.06, 8.88) * mm, "end": v(5.1, 9.46) * mm});
            skLineSegment(sketch, "E19.19.6", {"start": v(7.5, 8.24) * mm, "end": v(7.8, 8.58) * mm});
            skArc(sketch, "E19.19.7", {"start": v(5.68, 10.57) * mm, "mid": v(5.37, 10.6) * mm, "end": v(5.13, 10.4) * mm});
            skArc(sketch, "E19.19.8", {"start": v(4.93, 10) * mm, "mid": v(4.91, 9.7) * mm, "end": v(5.1, 9.46) * mm});
            skArc(sketch, "E19.19.9", {"start": v(7.8, 8.58) * mm, "mid": v(7.9, 8.87) * mm, "end": v(7.76, 9.15) * mm});
            skLineSegment(sketch, "E19.19.10", {"start": v(4.93, 10) * mm, "end": v(5.13, 10.4) * mm});
            skArc(sketch, "E19.19.11", {"start": v(6.94, 8.2) * mm, "mid": v(7.23, 8.11) * mm, "end": v(7.5, 8.24) * mm});
            skPoint(sketch, "E19.20.0", {"position": v(4.57, 9.73) * mm});
            skPoint(sketch, "E19.20.1", {"position": v(1.7, 10.61) * mm});
            skPoint(sketch, "E19.20.2", {"position": v(5.1, 10.86) * mm});
            skPoint(sketch, "E19.20.3", {"position": v(1.9, 11.85) * mm});
            skArc(sketch, "E19.20.4", {"start": v(4.72, 11.03) * mm, "mid": v(3.54, 11.47) * mm, "end": v(2.31, 11.77) * mm});
            skArc(sketch, "E19.20.5", {"start": v(4.22, 9.89) * mm, "mid": v(3.17, 10.27) * mm, "end": v(2.09, 10.55) * mm});
            skLineSegment(sketch, "E19.20.6", {"start": v(4.73, 10.09) * mm, "end": v(4.93, 10.5) * mm});
            skArc(sketch, "E19.20.7", {"start": v(2.31, 11.77) * mm, "mid": v(2, 11.71) * mm, "end": v(1.84, 11.45) * mm});
            skArc(sketch, "E19.20.8", {"start": v(1.77, 11) * mm, "mid": v(1.84, 10.7) * mm, "end": v(2.09, 10.55) * mm});
            skArc(sketch, "E19.20.9", {"start": v(4.93, 10.5) * mm, "mid": v(4.94, 10.8) * mm, "end": v(4.72, 11.03) * mm});
            skLineSegment(sketch, "E19.20.10", {"start": v(1.77, 11) * mm, "end": v(1.84, 11.45) * mm});
            skArc(sketch, "E19.20.11", {"start": v(4.22, 9.89) * mm, "mid": v(4.51, 9.88) * mm, "end": v(4.73, 10.09) * mm});
            skSolve(sketch);
        }
        {
            var Q0;
            Q0 = qSketchRegion(id + "F16", true);
            extrude(context, id + "F17", {"entities" : qUnion([Q0]), "operationType" : NewBodyOperationType.ADD, "oppositeDirection" : true, "depth" : 9 * mm});
        }
        {
            var Q0;
            Q0=makeQuery(id+"F1.opExtrude","CAP_FACE",FACE,{"disambiguationData":[OSD([sQuery(id+"F0.wireOp",EDGE,"E0")])],"isStart":true});
            var sketch = newSketch(context, id + "F18", { "sketchPlane" : qUnion([Q0])});
            skArc(sketch, "E20", {"start": v(2.86, 13.45) * mm, "mid": v(0, 13.75) * mm, "end": v(-2.86, 13.45) * mm});
            skLineSegment(sketch, "E21", {"start": v(-2.86, 13.45) * mm, "end": v(-2.04, 9.58) * mm});
            skLineSegment(sketch, "E22", {"start": v(2.86, 13.45) * mm, "end": v(2.04, 9.58) * mm});
            skArc(sketch, "E23", {"start": v(0.06, 8) * mm, "mid": v(0, 8) * mm, "end": v(-0.06, 8) * mm});
            skPoint(sketch, "E24.visualSharp", {"position": v(-1.66, 7.83) * mm});
            skArc(sketch, "E24.filletArc", {"start": v(-2.04, 9.58) * mm, "mid": v(-1.33, 8.44) * mm, "end": v(-0.06, 8) * mm});
            skPoint(sketch, "E25.visualSharp", {"position": v(1.66, 7.83) * mm});
            skArc(sketch, "E25.filletArc", {"start": v(0.06, 8) * mm, "mid": v(1.33, 8.44) * mm, "end": v(2.04, 9.58) * mm});
            skPoint(sketch, "E26.1.0", {"position": v(6.17, 5.09) * mm});
            skArc(sketch, "E26.1.1", {"start": v(7.13, 3.64) * mm, "mid": v(8.1, 2.71) * mm, "end": v(9.44, 2.62) * mm});
            skPoint(sketch, "E26.1.2", {"position": v(7.7, 2.14) * mm});
            skArc(sketch, "E26.1.3", {"start": v(7.56, 6.23) * mm, "mid": v(6.87, 5.08) * mm, "end": v(7.07, 3.75) * mm});
            skLineSegment(sketch, "E26.1.4", {"start": v(13.25, 3.67) * mm, "end": v(9.44, 2.62) * mm});
            skLineSegment(sketch, "E26.1.5", {"start": v(10.6, 8.75) * mm, "end": v(7.56, 6.23) * mm});
            skArc(sketch, "E26.1.6", {"start": v(13.25, 3.67) * mm, "mid": v(12.2, 6.35) * mm, "end": v(10.6, 8.75) * mm});
            skArc(sketch, "E26.1.7", {"start": v(7.13, 3.64) * mm, "mid": v(7.1, 3.7) * mm, "end": v(7.07, 3.75) * mm});
            skPoint(sketch, "E26.2.0", {"position": v(7.36, -3.13) * mm});
            skArc(sketch, "E26.2.1", {"start": v(6.52, -4.64) * mm, "mid": v(6.15, -5.93) * mm, "end": v(6.68, -7.17) * mm});
            skPoint(sketch, "E26.2.2", {"position": v(5.46, -5.85) * mm});
            skArc(sketch, "E26.2.3", {"start": v(9.02, -3.83) * mm, "mid": v(7.68, -3.75) * mm, "end": v(6.6, -4.54) * mm});
            skLineSegment(sketch, "E26.2.4", {"start": v(9.38, -10.06) * mm, "end": v(6.68, -7.17) * mm});
            skLineSegment(sketch, "E26.2.5", {"start": v(12.66, -5.37) * mm, "end": v(9.02, -3.83) * mm});
            skArc(sketch, "E26.2.6", {"start": v(9.38, -10.06) * mm, "mid": v(11.26, -7.89) * mm, "end": v(12.66, -5.37) * mm});
            skArc(sketch, "E26.2.7", {"start": v(6.52, -4.64) * mm, "mid": v(6.55, -4.59) * mm, "end": v(6.6, -4.54) * mm});
            skPoint(sketch, "E26.3.0", {"position": v(0.63, -7.98) * mm});
            skArc(sketch, "E26.3.1", {"start": v(-1.1, -7.92) * mm, "mid": v(-2.42, -8.2) * mm, "end": v(-3.27, -9.24) * mm});
            skPoint(sketch, "E26.3.2", {"position": v(-2.67, -7.54) * mm});
            skArc(sketch, "E26.3.3", {"start": v(0.77, -9.77) * mm, "mid": v(0.22, -8.54) * mm, "end": v(-0.98, -7.94) * mm});
            skLineSegment(sketch, "E26.3.4", {"start": v(-4.59, -12.96) * mm, "end": v(-3.27, -9.24) * mm});
            skLineSegment(sketch, "E26.3.5", {"start": v(1.08, -13.7) * mm, "end": v(0.77, -9.77) * mm});
            skArc(sketch, "E26.3.6", {"start": v(-4.59, -12.96) * mm, "mid": v(-1.8, -13.63) * mm, "end": v(1.08, -13.7) * mm});
            skArc(sketch, "E26.3.7", {"start": v(-1.1, -7.92) * mm, "mid": v(-1.04, -7.93) * mm, "end": v(-0.98, -7.94) * mm});
            skPoint(sketch, "E26.4.0", {"position": v(-6.78, -4.24) * mm});
            skArc(sketch, "E26.4.1", {"start": v(-7.54, -2.68) * mm, "mid": v(-8.39, -1.63) * mm, "end": v(-9.7, -1.36) * mm});
            skPoint(sketch, "E26.4.2", {"position": v(-7.92, -1.11) * mm});
            skArc(sketch, "E26.4.3", {"start": v(-8.3, -5.2) * mm, "mid": v(-7.48, -4.14) * mm, "end": v(-7.5, -2.8) * mm});
            skLineSegment(sketch, "E26.4.4", {"start": v(-13.62, -1.91) * mm, "end": v(-9.7, -1.36) * mm});
            skLineSegment(sketch, "E26.4.5", {"start": v(-11.66, -7.29) * mm, "end": v(-8.3, -5.2) * mm});
            skArc(sketch, "E26.4.6", {"start": v(-13.62, -1.91) * mm, "mid": v(-12.92, -4.7) * mm, "end": v(-11.66, -7.29) * mm});
            skArc(sketch, "E26.4.7", {"start": v(-7.54, -2.68) * mm, "mid": v(-7.52, -2.74) * mm, "end": v(-7.5, -2.8) * mm});
            skLineSegment(sketch, "E26.anchor1", {"start": v(0, 0) * mm, "end": v(-1.66, 7.83) * mm, "construction": true});
            skLineSegment(sketch, "E26.anchor2", {"start": v(0, 0) * mm, "end": v(-6.78, -4.24) * mm, "construction": true});
            skSolve(sketch);
        }
        {
            var Q0;
            Q0 = qSketchRegion(id + "F18", true);
            extrude(context, id + "F19", {"entities" : qUnion([Q0]), "operationType" : NewBodyOperationType.REMOVE, "oppositeDirection" : true, "depth" : 2.5 * mm});
        }
        {
            var Q0;
            Q0=makeQuery(id+"F19.boolean.opBoolean","COPY",EDGE,{"derivedFrom":makeQuery(id+"F19.opExtrude","CAP_EDGE",EDGE,{"disambiguationData":[OSD([sQuery(id+"F18.wireOp",EDGE,"E26.1.5")])],"isStart":false})});
            var Q1;
            Q1=makeQuery(id+"F19.boolean.opBoolean","COPY",EDGE,{"derivedFrom":makeQuery(id+"F19.opExtrude","CAP_EDGE",EDGE,{"disambiguationData":[OSD([sQuery(id+"F18.wireOp",EDGE,"E26.1.4")])],"isStart":false})});
            var Q2;
            Q2=makeQuery(id+"F19.boolean.opBoolean","COPY",EDGE,{"derivedFrom":makeQuery(id+"F19.opExtrude","CAP_EDGE",EDGE,{"disambiguationData":[OSD([sQuery(id+"F18.wireOp",EDGE,"E22")])],"isStart":false})});
            var Q3;
            Q3=makeQuery(id+"F19.boolean.opBoolean","COPY",EDGE,{"derivedFrom":makeQuery(id+"F19.opExtrude","CAP_EDGE",EDGE,{"disambiguationData":[OSD([sQuery(id+"F18.wireOp",EDGE,"E21")])],"isStart":false})});
            var Q4;
            Q4=makeQuery(id+"F19.boolean.opBoolean","COPY",EDGE,{"derivedFrom":makeQuery(id+"F19.opExtrude","CAP_EDGE",EDGE,{"disambiguationData":[OSD([sQuery(id+"F18.wireOp",EDGE,"E26.2.5")])],"isStart":false})});
            var Q5;
            Q5=makeQuery(id+"F19.boolean.opBoolean","COPY",EDGE,{"derivedFrom":makeQuery(id+"F19.opExtrude","CAP_EDGE",EDGE,{"disambiguationData":[OSD([sQuery(id+"F18.wireOp",EDGE,"E26.2.4")])],"isStart":false})});
            var Q6;
            Q6=makeQuery(id+"F19.boolean.opBoolean","COPY",EDGE,{"derivedFrom":makeQuery(id+"F19.opExtrude","CAP_EDGE",EDGE,{"disambiguationData":[OSD([sQuery(id+"F18.wireOp",EDGE,"E26.3.5")])],"isStart":false})});
            var Q7;
            Q7=makeQuery(id+"F19.boolean.opBoolean","COPY",EDGE,{"derivedFrom":makeQuery(id+"F19.opExtrude","CAP_EDGE",EDGE,{"disambiguationData":[OSD([sQuery(id+"F18.wireOp",EDGE,"E26.3.4")])],"isStart":false})});
            var Q8;
            Q8=makeQuery(id+"F19.boolean.opBoolean","COPY",EDGE,{"derivedFrom":makeQuery(id+"F19.opExtrude","CAP_EDGE",EDGE,{"disambiguationData":[OSD([sQuery(id+"F18.wireOp",EDGE,"E26.4.5")])],"isStart":false})});
            var Q9;
            Q9=makeQuery(id+"F19.boolean.opBoolean","COPY",EDGE,{"derivedFrom":makeQuery(id+"F19.opExtrude","CAP_EDGE",EDGE,{"disambiguationData":[OSD([sQuery(id+"F18.wireOp",EDGE,"E26.4.4")])],"isStart":false})});
            fillet(context, id + "F20", {"entities" : qUnion([Q0, Q1, Q2, Q3, Q4, Q5, Q6, Q7, Q8, Q9]), "radius" : 1.5 * mm, "tangentPropagation" : true, "allowEdgeOverflow" : false});
        }
        {
            var Q0;
            Q0=makeQuery(id+"F1.opExtrude","CAP_FACE",FACE,{"disambiguationData":[OSD([sQuery(id+"F0.wireOp",EDGE,"E0")])],"isStart":true});
            var sketch = newSketch(context, id + "F21", { "sketchPlane" : qUnion([Q0])});
            skCircle(sketch, "E27", {"center": v(0, 0) * mm, "radius": 4 * mm});
            skSolve(sketch);
        }
        {
            var Q0;
            Q0 = qSketchRegion(id + "F21", true);
            extrude(context, id + "F22", {"entities" : qUnion([Q0]), "operationType" : NewBodyOperationType.REMOVE, "oppositeDirection" : true, "depth" : 5 * mm});
        }
        {
            var Q0;
            Q0=qCreatedBy(makeId("Right.planeOp"),FACE);
            var sketch = newSketch(context, id + "F23", { "sketchPlane" : qUnion([Q0])});
            skLineSegment(sketch, "E28", {"start": v(0, 0) * mm, "end": v(0, 44) * mm, "construction": true});
            skSolve(sketch);
        }
        {
            var Q0;
            Q0=sQuery(id+"F23.wireOp",EDGE,"E28");
            cPlane(context, id + "F24", {"entities" : qUnion([Q0]), "cplaneType" : CPlaneType.LINE_ANGLE, "offset" : 25 * mm, "angle" : 37 * degree, "width" : 150 * mm, "height" : 150 * mm});
        }
        {
            var Q0;
            Q0=qCreatedBy(id+"F24.planeOp",FACE);
            var sketch = newSketch(context, id + "F25", { "sketchPlane" : qUnion([Q0])});
            skLineSegment(sketch, "E29.bottom", {"start": v(3.5, 2.5) * mm, "end": v(-3.5, 2.5) * mm});
            skLineSegment(sketch, "E29.top", {"start": v(5, 0) * mm, "end": v(-5, 0) * mm});
            skLineSegment(sketch, "E29.left", {"start": v(5, 1) * mm, "end": v(5, 0) * mm});
            skLineSegment(sketch, "E29.right", {"start": v(-5, 1) * mm, "end": v(-5, 0) * mm});
            skPoint(sketch, "E30.visualSharp", {"position": v(5, 2.5) * mm});
            skArc(sketch, "E30.filletArc", {"start": v(5, 1) * mm, "mid": v(4.56, 2.06) * mm, "end": v(3.5, 2.5) * mm});
            skPoint(sketch, "E31.visualSharp", {"position": v(-5, 2.5) * mm});
            skArc(sketch, "E31.filletArc", {"start": v(-3.5, 2.5) * mm, "mid": v(-4.56, 2.06) * mm, "end": v(-5, 1) * mm});
            skSolve(sketch);
        }
        {
            var Q0;
            Q0 = qSketchRegion(id + "F25", true);
            extrude(context, id + "F26", {"entities" : qUnion([Q0]), "operationType" : NewBodyOperationType.REMOVE, "oppositeDirection" : true, "depth" : 25 * mm, "hasSecondDirection" : true, "secondDirectionOppositeDirection" : true, "secondDirectionDepth" : 8 * mm});
        }
        {
            var Q0;
            Q0=makeQuery(id+"F26.boolean.opBoolean","COPY",EDGE,{"derivedFrom":makeQuery(id+"F26.opExtrude","CAP_EDGE",EDGE,{"disambiguationData":[OSD([sQuery(id+"F25.wireOp",EDGE,"E29.left")])],"isStart":true})});
            var Q1;
            Q1=makeQuery(id+"F26.boolean.opBoolean","COPY",EDGE,{"derivedFrom":makeQuery(id+"F26.opExtrude","CAP_EDGE",EDGE,{"disambiguationData":[OSD([sQuery(id+"F25.wireOp",EDGE,"E29.right")])],"isStart":true})});
            fillet(context, id + "F27", {"entities" : qUnion([Q0, Q1]), "radius" : 2 * mm, "tangentPropagation" : true, "allowEdgeOverflow" : false});
        }
    });
